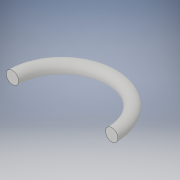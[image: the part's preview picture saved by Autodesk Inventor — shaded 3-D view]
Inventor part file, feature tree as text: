
AUTODESK INVENTOR PART (.ipt)
format: ipt  version: 2017 (Build 210142000, 142)  size: 133,632 bytes
history: native  units: in
note: dims shown in document units (in); Inventor stores cm internally (conversion verified against a paired STEP export)
features: sketch x2, sweep x1
ambient origin geometry x8: Origin, YZ Plane, XZ Plane, XY Plane, X Axis, Y Axis, Z Axis, Center Point
bodies: Solid1 (feature_tree)
feature tree (3):
  sweep  "Sweep1"
  sketch  "Sketch3"  dims[d2=2.0in d3=2.0in]
  sketch  "Sketch4"  dims[d4=16.0in d6=16.0in d7=0.0in d8=0.0in]
